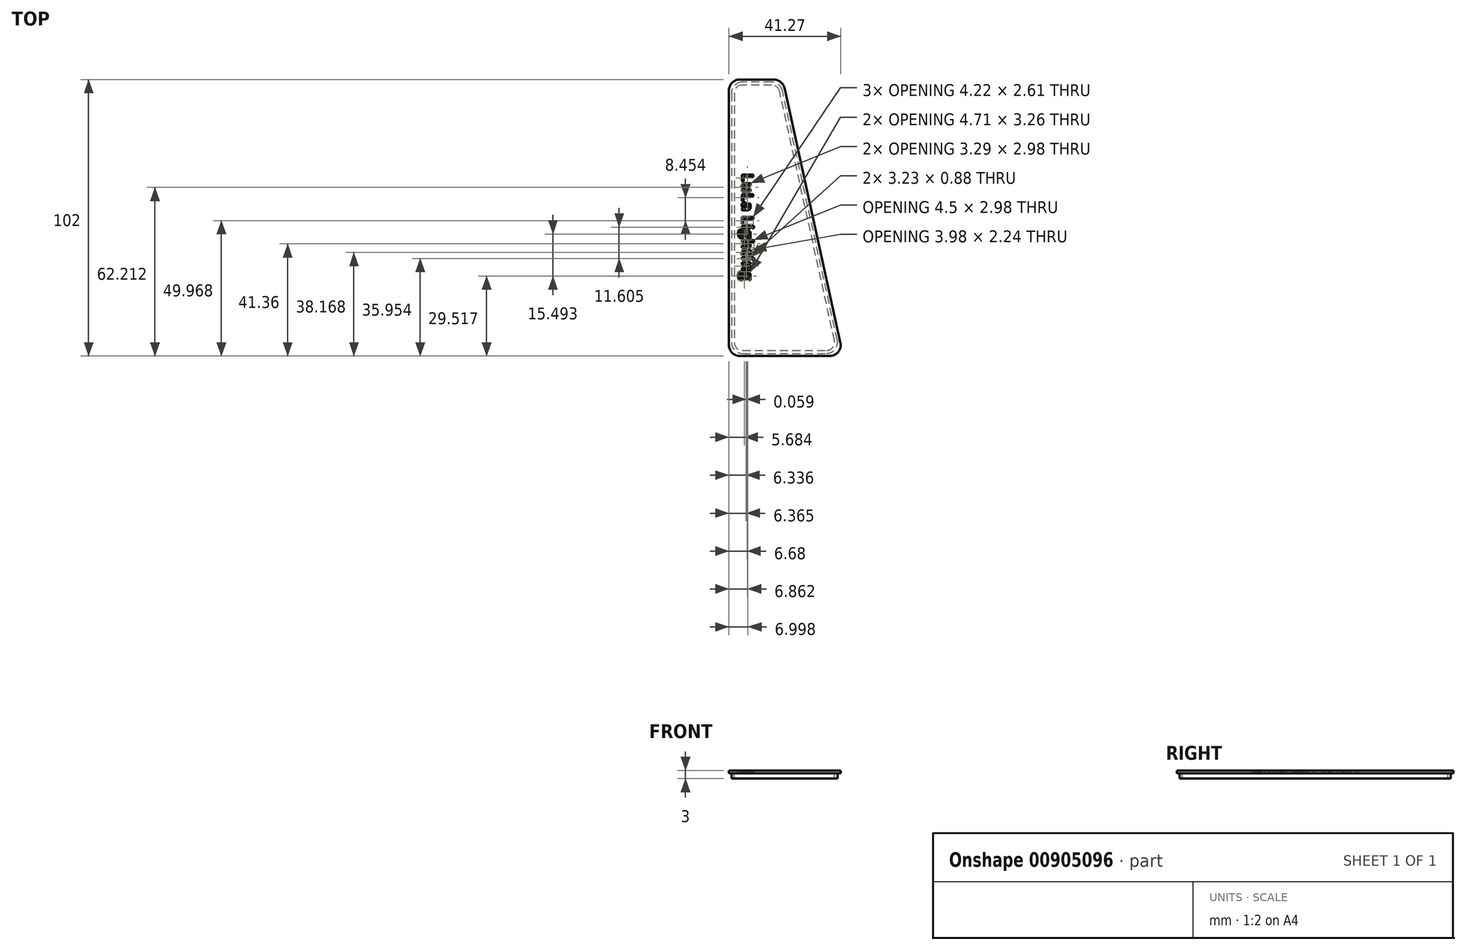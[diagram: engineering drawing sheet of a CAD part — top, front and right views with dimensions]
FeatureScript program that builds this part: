
annotation { "Feature Type Name" : "Feature", "Feature Type Description" : "" }
export const myFeature = defineFeature(function(context is Context, id is Id, definition is map)
    precondition{}
    {
        {
            var Q0;
            Q0=qCreatedBy(makeId("Top.planeOp"),FACE);
            var sketch = newSketch(context, id + "F0", { "sketchPlane" : qUnion([Q0])});
            skLineSegment(sketch, "E0", {"start": v(0, 75.83) * mm, "end": v(0, -16.17) * mm});
            skLineSegment(sketch, "E1", {"start": v(4, -20.17) * mm, "end": v(35.02, -20.17) * mm});
            skLineSegment(sketch, "E2", {"start": v(38.93, -15.3) * mm, "end": v(18.7, 76.7) * mm});
            skLineSegment(sketch, "E3", {"start": v(14.78, 79.83) * mm, "end": v(4, 79.83) * mm});
            skLineSegment(sketch, "E4.0", {"start": v(-1, 76.83) * mm, "end": v(-1, -17.17) * mm});
            skLineSegment(sketch, "E4.1", {"start": v(15.59, 80.83) * mm, "end": v(3, 80.83) * mm});
            skLineSegment(sketch, "E4.2", {"start": v(40.17, -16.3) * mm, "end": v(19.5, 77.7) * mm});
            skLineSegment(sketch, "E4.3", {"start": v(3, -21.17) * mm, "end": v(36.27, -21.17) * mm});
            skPoint(sketch, "E5.visualSharp", {"position": v(18, 79.83) * mm});
            skArc(sketch, "E5.filletArc", {"start": v(18.7, 76.7) * mm, "mid": v(17.3, 78.95) * mm, "end": v(14.78, 79.83) * mm});
            skPoint(sketch, "E6.visualSharp", {"position": v(18.8, 80.83) * mm});
            skArc(sketch, "E6.filletArc", {"start": v(19.5, 77.7) * mm, "mid": v(18.1, 79.95) * mm, "end": v(15.59, 80.83) * mm});
            skPoint(sketch, "E7.visualSharp", {"position": v(0, 79.83) * mm});
            skArc(sketch, "E7.filletArc", {"start": v(4, 79.83) * mm, "mid": v(1.17, 78.66) * mm, "end": v(0, 75.83) * mm});
            skPoint(sketch, "E8.visualSharp", {"position": v(-1, 80.83) * mm});
            skArc(sketch, "E8.filletArc", {"start": v(3, 80.83) * mm, "mid": v(0.17, 79.66) * mm, "end": v(-1, 76.83) * mm});
            skPoint(sketch, "E9.visualSharp", {"position": v(0, -20.17) * mm});
            skArc(sketch, "E9.filletArc", {"start": v(0, -16.17) * mm, "mid": v(1.17, -19) * mm, "end": v(4, -20.17) * mm});
            skPoint(sketch, "E10.visualSharp", {"position": v(-1, -21.17) * mm});
            skArc(sketch, "E10.filletArc", {"start": v(-1, -17.17) * mm, "mid": v(0.17, -20) * mm, "end": v(3, -21.17) * mm});
            skPoint(sketch, "E11.visualSharp", {"position": v(40, -20.17) * mm});
            skArc(sketch, "E11.filletArc", {"start": v(35.02, -20.17) * mm, "mid": v(38.14, -18.67) * mm, "end": v(38.93, -15.3) * mm});
            skPoint(sketch, "E12.visualSharp", {"position": v(41.24, -21.17) * mm});
            skArc(sketch, "E12.filletArc", {"start": v(36.27, -21.17) * mm, "mid": v(39.39, -19.67) * mm, "end": v(40.17, -16.3) * mm});
            skPoint(sketch, "E13.start.orphan", {"position": v(18.2, 0) * mm});
            skArc(sketch, "E14.0", {"start": v(4, 78.83) * mm, "mid": v(1.88, 77.96) * mm, "end": v(1, 75.83) * mm});
            skLineSegment(sketch, "E14.1", {"start": v(14.78, 78.83) * mm, "end": v(4, 78.83) * mm});
            skLineSegment(sketch, "E14.2", {"start": v(1, 75.83) * mm, "end": v(1, -16.17) * mm});
            skArc(sketch, "E14.3", {"start": v(17.71, 76.48) * mm, "mid": v(16.66, 78.17) * mm, "end": v(14.78, 78.83) * mm});
            skArc(sketch, "E14.4", {"start": v(1, -16.17) * mm, "mid": v(1.88, -18.29) * mm, "end": v(4, -19.17) * mm});
            skLineSegment(sketch, "E14.5", {"start": v(4, -19.17) * mm, "end": v(35.02, -19.17) * mm});
            skArc(sketch, "E14.6", {"start": v(35.02, -19.17) * mm, "mid": v(37.36, -18.04) * mm, "end": v(37.95, -15.52) * mm});
            skLineSegment(sketch, "E14.7", {"start": v(37.95, -15.52) * mm, "end": v(17.71, 76.48) * mm});
            skArc(sketch, "E15.0", {"start": v(4, 79.88) * mm, "mid": v(1.14, 78.7) * mm, "end": v(-0.05, 75.83) * mm});
            skLineSegment(sketch, "E15.1", {"start": v(14.78, 79.88) * mm, "end": v(4, 79.88) * mm});
            skLineSegment(sketch, "E15.2", {"start": v(-0.05, 75.83) * mm, "end": v(-0.05, -16.17) * mm});
            skArc(sketch, "E15.3", {"start": v(18.74, 76.7) * mm, "mid": v(17.32, 79) * mm, "end": v(14.78, 79.88) * mm});
            skArc(sketch, "E15.4", {"start": v(-0.05, -16.17) * mm, "mid": v(1.14, -19.03) * mm, "end": v(4, -20.22) * mm});
            skLineSegment(sketch, "E15.5", {"start": v(4, -20.22) * mm, "end": v(35.02, -20.22) * mm});
            skArc(sketch, "E15.6", {"start": v(35.02, -20.22) * mm, "mid": v(38.18, -18.7) * mm, "end": v(38.98, -15.3) * mm});
            skLineSegment(sketch, "E15.7", {"start": v(38.98, -15.3) * mm, "end": v(18.74, 76.7) * mm});
            skSolve(sketch);
        }
        {
            var Q0;
            Q0=makeQuery(id+"F0.imprint","IMPRINT",FACE,{"disambiguationData":[TD([[makeQuery(id+"F0.imprint","IMPRINT",EDGE,{"derivedFrom":sQuery(id+"F0.wireOp",EDGE,"E4.0")}),1.0]])]});
            var Q1;
            Q1=makeQuery(id+"F0.imprint","IMPRINT",FACE,{"disambiguationData":[TD([[makeQuery(id+"F0.imprint","IMPRINT",EDGE,{"derivedFrom":sQuery(id+"F0.wireOp",EDGE,"E14.0")}),1.0]])]});
            extrude(context, id + "F1", {"entities" : qUnion([Q0, Q1]), "oppositeDirection" : true, "depth" : 1 * mm, "offsetDistance" : 25 * mm});
        }
        {
            var Q0;
            Q0=makeQuery(id+"F0.imprint","IMPRINT",FACE,{"disambiguationData":[TD([[makeQuery(id+"F0.imprint","IMPRINT",EDGE,{"derivedFrom":sQuery(id+"F0.wireOp",EDGE,"E0")}),1.0]])]});
            var Q1;
            Q1=makeQuery(id+"F0.imprint","IMPRINT",FACE,{"disambiguationData":[TD([[makeQuery(id+"F0.imprint","IMPRINT",EDGE,{"derivedFrom":sQuery(id+"F0.wireOp",EDGE,"E0")}),-1.0]])]});
            extrude(context, id + "F2", {"entities" : qUnion([Q0, Q1]), "operationType" : NewBodyOperationType.ADD, "oppositeDirection" : true, "depth" : 3 * mm, "offsetDistance" : 25 * mm});
        }
        {
            var Q0;
            Q0=makeQuery(id+"F0.imprint","IMPRINT",FACE,{"disambiguationData":[TD([[makeQuery(id+"F0.imprint","IMPRINT",EDGE,{"derivedFrom":sQuery(id+"F0.wireOp",EDGE,"E14.0")}),1.0]])]});
            var sketch = newSketch(context, id + "F3", { "sketchPlane" : qUnion([Q0])});
            skText(sketch, "E16", { "text": "LuLa Lighting\n", "fontName": "OpenSans-Bold.ttf"});
            const initialGuessF3  = {"E16": [0.00375, 0.04632, 0, -1, 0.00426]};
            skSetInitialGuess(sketch, initialGuessF3);
            skSolve(sketch);
        }
        {
            var Q0;
            Q0 = qSketchRegion(id + "F3", true);
            extrude(context, id + "F4", {"entities" : qUnion([Q0]), "operationType" : NewBodyOperationType.REMOVE, "oppositeDirection" : true, "depth" : 25 * mm, "offsetDistance" : 25 * mm});
        }
    });
